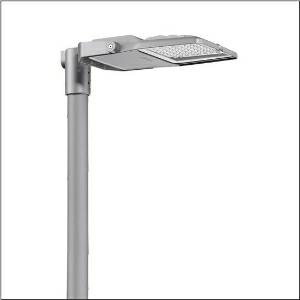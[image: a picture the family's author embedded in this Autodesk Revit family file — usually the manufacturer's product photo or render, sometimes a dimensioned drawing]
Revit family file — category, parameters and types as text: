
# Revit family: floodlight_fl_21_iq_mini___pl64_5xa7771d2e3a_d262
name_source: partatom
category: Lighting Fixtures
units: mm (PartAtom-declared; Revit-internal decimal feet)

## family parameters
Cut with Voids When Loaded = No
Host = Face
Light Source = No
Part Type = Normal
Room Calculation Point = No
Round Connector Dimension = Use Diameter
Shared = No

## types (1)
- --- (1 x LED, 17220 lm, 143 W, 3000K)
    Apparent Load = 143 VA
    CIE Flux Codes = 28 80 98 100 100
    Color Rendering = 70
    Color Temperature = 3000K
    Default Elevation = 1800 mm
    Description = Floodlight FL 21 iQ mini, floodlight, primary light control with lens, of PMMA, primary optical cover: protective disc, of toughened safety glass, transparent, light distribution: PL64, light emission: direct distribution, installation type: surface-mounted, lamps: LED, High Power LED, rated values: 17.220lm | 143W | 120,4lm/W (begin service life); end service life: 17.220lm | 151,6W; at 50% lumin. flux: 8.610lm | 60,6W | 142,1lm/W, colour temperature: 3000K, colour rendering: CRI > 70, light colour: 730, light setting 1 begin service life: 100% | 17.220lm | 143W | 120,4lm/W | 3.000K, light setting 1 end service life: 151,6W, further light settings possible, control: Auto-Match, Temp-Guard, Lumen-Switch, Night-Set, Smart-Wire, Light-Fading, Desk-Remote (wireless, voltage-free reading and setting of iQ features in the workshop via application-optimized NFC function/RFID function), optimised constant luminous flux control (CLO 2.0), pre-setting: linear dimming characteristic, with terminal, 6-pole, mains connection: 220..240V, AC, 50/60Hz, luminaire housing, of diecast aluminium, powder-coated, SITECO metallic grey (DB 702S), corrosivity category C5 mid according to DIN EN ISO 12944suitable for swimming poolschlorine-resistant, sealing non-destructively replaceable, please order mast flange separately, mast bracket, of steel, galvanised, powder-coated, SITECO metallic grey (DB 702S), protection rating (complete): IP66, insulation class (complete): insulation class II (safety insulation), certification: CE, ENEC, VDE, protection symbol: D, impact resistance: IK08, permissible operating ambient temperature: -40..+40°C, permissible operating ambient temperature for outdoor applications: -40..+50°C, standard: DIN EN 12944, LABS conformity tested according to VDMA 24364:2018-05, packaging unit: 1 piece

Light Distribution: PL64
    Height = 70 mm
    Lamp = 1 x LED
    Lamp Light Flux = 17220 lm
    Lamp Power = 143 W
    Lamp count = 1
    Length = 485 mm
    Luminous efficacy = 120 lm/W
    Manufacturer = Siteco
    ModVariant = No
    Model = 5XA7771D2E3A
    Number of Poles = 1
    OnlyDefault = Yes
    Power Factor = 1
    Product Name = Floodlight FL 21 iQ mini | PL64
    Product group = floodlight | pylon annexe
    ProductGroupID = 6201
    Protection Class = Protection class II
    Protection Degree = IP 66
    RLX_Detail_Level = 1
    RLX_Emergency_Light_Flux = 0 lm
    RLX_Emergency_Type = 0
    RLX_Emergency_Type_DB = No
    RlxData = <blob elided: 101805 chars, md5=9db5a8b3>
    Socket = socket
    Standby Power = 0 W
    System Light Flux = 17220 lm
    System Power = 143 W
    Type Comments = factory setting: luminous flux: 100 % | dim-lin: 254 | 730 mA
    Type Image = l_1007125.jpg
    URL = http://relux.com
    VarID = @adj_165545
    Voltage = 0 V
    Weight = 0.00 kg
    Width = 337 mm

## geometry (parser evidence)
native form markers: Blend x4, Sweep x12
no freeform markers — native parametric forms only
